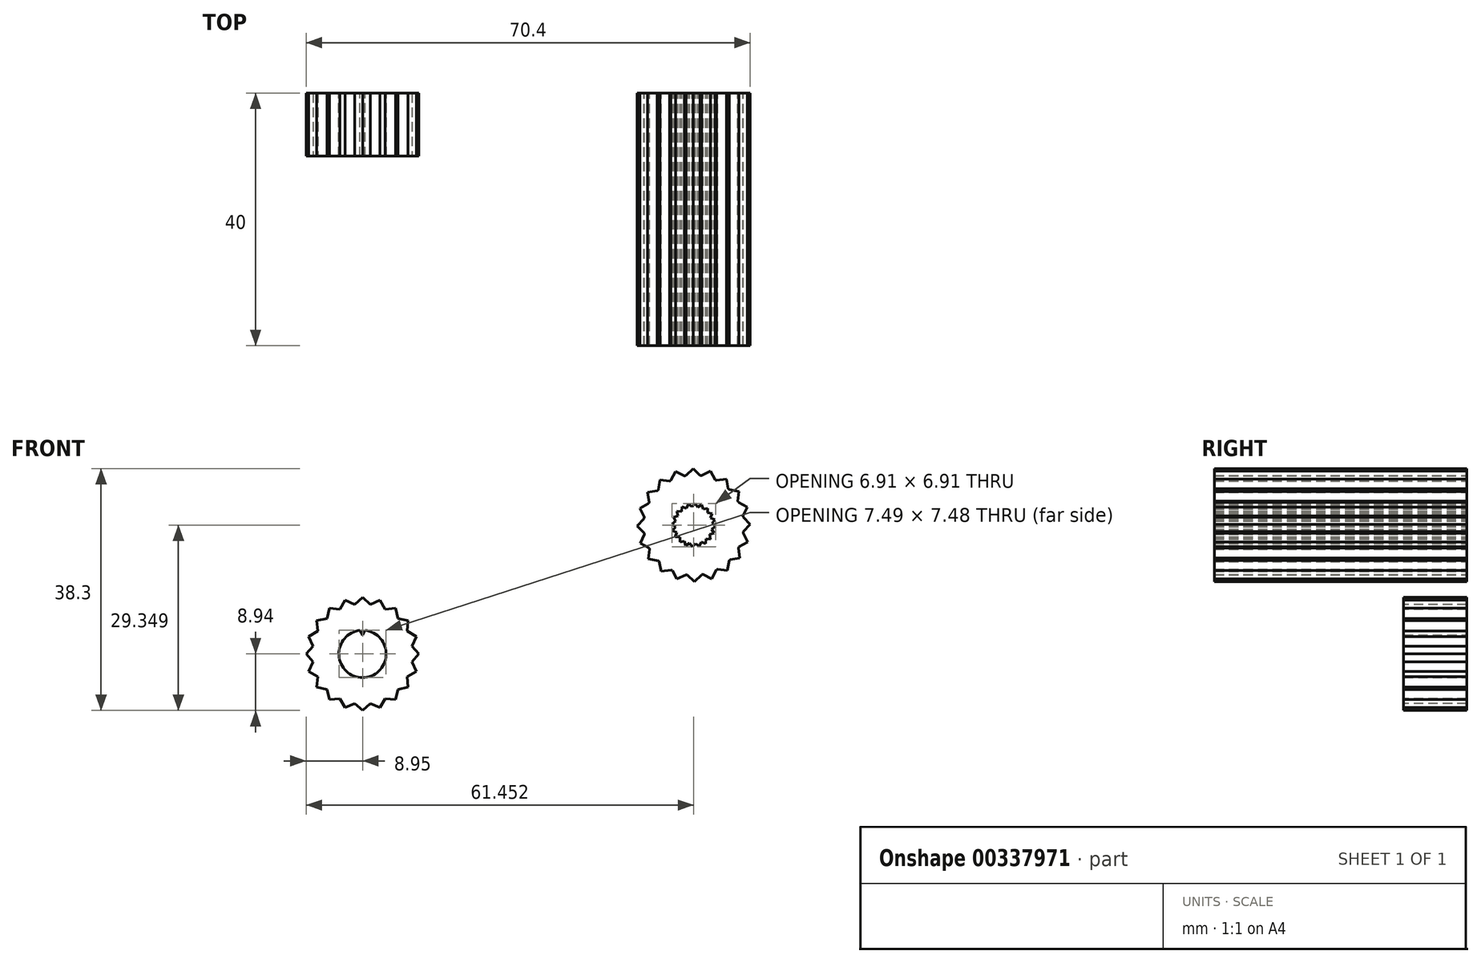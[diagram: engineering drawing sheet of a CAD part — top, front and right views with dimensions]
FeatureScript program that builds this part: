
annotation { "Feature Type Name" : "Feature", "Feature Type Description" : "" }
export const myFeature = defineFeature(function(context is Context, id is Id, definition is map)
    precondition{}
    {
        {
            var Q0;
            Q0=qCreatedBy(makeId("Front.planeOp"),FACE);
            var sketch = newSketch(context, id + "F0", { "sketchPlane" : qUnion([Q0])});
            skCircle(sketch, "E0", {"center": v(0, 0) * mm, "radius": 3 * mm});
            skCircle(sketch, "E1", {"center": v(0, 0) * mm, "radius": 7.95 * mm});
            skCircle(sketch, "E2", {"center": v(0, 0) * mm, "radius": 3.75 * mm});
            skCircle(sketch, "E3", {"center": v(0, 0) * mm, "radius": 8.95 * mm, "construction": true});
            skLineSegment(sketch, "E4", {"start": v(0, 8.95) * mm, "end": v(0, 0) * mm, "construction": true});
            skSolve(sketch);
        }
        {
            var Q0;
            Q0=makeQuery(id+"F0.imprint","IMPRINT",FACE,{"disambiguationData":[TD([[makeQuery(id+"F0.imprint","IMPRINT",EDGE,{"derivedFrom":sQuery(id+"F0.wireOp",EDGE,"E2")}),-1.0]])]});
            extrude(context, id + "F1", {"entities" : qUnion([Q0]), "depth" : 10 * mm});
        }
        {
            var Q0;
            Q0=makeQuery(id+"F1.opExtrude","CAP_FACE",FACE,{"disambiguationData":[OSD([sQuery(id+"F0.wireOp",EDGE,"E1"),sQuery(id+"F0.wireOp",EDGE,"E2")])],"isStart":false});
            var sketch = newSketch(context, id + "F2", { "sketchPlane" : qUnion([Q0])});
            skLineSegment(sketch, "E5", {"start": v(0, 7.95) * mm, "end": v(0, 0) * mm, "construction": true});
            skCircle(sketch, "E6.0", {"center": v(0, 0) * mm, "radius": 7.95 * mm});
            skLineSegment(sketch, "E7", {"start": v(-1.24, 7.85) * mm, "end": v(0, 8.95) * mm});
            skLineSegment(sketch, "E8", {"start": v(0, 8.95) * mm, "end": v(1.24, 7.85) * mm});
            skLineSegment(sketch, "E9", {"start": v(1.24, 7.85) * mm, "end": v(-1.24, 7.85) * mm});
            skLineSegment(sketch, "E10", {"start": v(0, 0) * mm, "end": v(-1.24, 7.85) * mm, "construction": true});
            skLineSegment(sketch, "E11", {"start": v(0, 0) * mm, "end": v(1.24, 7.85) * mm, "construction": true});
            skCircle(sketch, "E12", {"center": v(0, 0) * mm, "radius": 8.95 * mm, "construction": true});
            skLineSegment(sketch, "E13.1.0", {"start": v(-3.58, 7.06) * mm, "end": v(-2.74, 8.49) * mm});
            skLineSegment(sketch, "E13.1.1", {"start": v(-1.21, 7.83) * mm, "end": v(-3.58, 7.06) * mm});
            skLineSegment(sketch, "E13.1.2", {"start": v(-2.74, 8.49) * mm, "end": v(-1.21, 7.83) * mm});
            skLineSegment(sketch, "E13.2.0", {"start": v(-5.56, 5.59) * mm, "end": v(-5.2, 7.2) * mm});
            skLineSegment(sketch, "E13.2.1", {"start": v(-3.55, 7.05) * mm, "end": v(-5.56, 5.59) * mm});
            skLineSegment(sketch, "E13.2.2", {"start": v(-5.2, 7.2) * mm, "end": v(-3.55, 7.05) * mm});
            skLineSegment(sketch, "E13.3.0", {"start": v(-6.98, 3.57) * mm, "end": v(-7.14, 5.22) * mm});
            skLineSegment(sketch, "E13.3.1", {"start": v(-5.52, 5.59) * mm, "end": v(-6.98, 3.57) * mm});
            skLineSegment(sketch, "E13.3.2", {"start": v(-7.14, 5.22) * mm, "end": v(-5.52, 5.59) * mm});
            skLineSegment(sketch, "E13.4.0", {"start": v(-7.72, 1.22) * mm, "end": v(-8.38, 2.74) * mm});
            skLineSegment(sketch, "E13.4.1", {"start": v(-6.95, 3.58) * mm, "end": v(-7.72, 1.22) * mm});
            skLineSegment(sketch, "E13.4.2", {"start": v(-8.38, 2.74) * mm, "end": v(-6.95, 3.58) * mm});
            skLineSegment(sketch, "E13.5.0", {"start": v(-7.69, -1.25) * mm, "end": v(-8.78, 0) * mm});
            skLineSegment(sketch, "E13.5.1", {"start": v(-7.69, 1.24) * mm, "end": v(-7.69, -1.25) * mm});
            skLineSegment(sketch, "E13.5.2", {"start": v(-8.78, 0) * mm, "end": v(-7.69, 1.24) * mm});
            skLineSegment(sketch, "E13.6.0", {"start": v(-6.9, -3.59) * mm, "end": v(-8.32, -2.74) * mm});
            skLineSegment(sketch, "E13.6.1", {"start": v(-7.66, -1.22) * mm, "end": v(-6.9, -3.59) * mm});
            skLineSegment(sketch, "E13.6.2", {"start": v(-8.32, -2.74) * mm, "end": v(-7.66, -1.22) * mm});
            skLineSegment(sketch, "E13.7.0", {"start": v(-5.42, -5.56) * mm, "end": v(-7.04, -5.2) * mm});
            skLineSegment(sketch, "E13.7.1", {"start": v(-6.88, -3.55) * mm, "end": v(-5.42, -5.56) * mm});
            skLineSegment(sketch, "E13.7.2", {"start": v(-7.04, -5.2) * mm, "end": v(-6.88, -3.55) * mm});
            skLineSegment(sketch, "E13.8.0", {"start": v(-3.4, -6.99) * mm, "end": v(-5.06, -7.15) * mm});
            skLineSegment(sketch, "E13.8.1", {"start": v(-5.42, -5.53) * mm, "end": v(-3.4, -6.99) * mm});
            skLineSegment(sketch, "E13.8.2", {"start": v(-5.06, -7.15) * mm, "end": v(-5.42, -5.53) * mm});
            skLineSegment(sketch, "E13.9.0", {"start": v(-1.05, -7.72) * mm, "end": v(-2.57, -8.38) * mm});
            skLineSegment(sketch, "E13.9.1", {"start": v(-3.42, -6.95) * mm, "end": v(-1.05, -7.72) * mm});
            skLineSegment(sketch, "E13.9.2", {"start": v(-2.57, -8.38) * mm, "end": v(-3.42, -6.95) * mm});
            skLineSegment(sketch, "E13.10.0", {"start": v(1.41, -7.7) * mm, "end": v(0.17, -8.79) * mm});
            skLineSegment(sketch, "E13.10.1", {"start": v(-1.07, -7.7) * mm, "end": v(1.41, -7.7) * mm});
            skLineSegment(sketch, "E13.10.2", {"start": v(0.17, -8.79) * mm, "end": v(-1.07, -7.7) * mm});
            skLineSegment(sketch, "E13.11.0", {"start": v(3.75, -6.9) * mm, "end": v(2.9, -8.33) * mm});
            skLineSegment(sketch, "E13.11.1", {"start": v(1.39, -7.67) * mm, "end": v(3.75, -6.9) * mm});
            skLineSegment(sketch, "E13.11.2", {"start": v(2.9, -8.33) * mm, "end": v(1.39, -7.67) * mm});
            skLineSegment(sketch, "E13.12.0", {"start": v(5.73, -5.43) * mm, "end": v(5.37, -7.04) * mm});
            skLineSegment(sketch, "E13.12.1", {"start": v(3.72, -6.89) * mm, "end": v(5.73, -5.43) * mm});
            skLineSegment(sketch, "E13.12.2", {"start": v(5.37, -7.04) * mm, "end": v(3.72, -6.89) * mm});
            skLineSegment(sketch, "E13.13.0", {"start": v(7.15, -3.41) * mm, "end": v(7.31, -5.06) * mm});
            skLineSegment(sketch, "E13.13.1", {"start": v(5.7, -5.42) * mm, "end": v(7.15, -3.41) * mm});
            skLineSegment(sketch, "E13.13.2", {"start": v(7.31, -5.06) * mm, "end": v(5.7, -5.42) * mm});
            skLineSegment(sketch, "E13.14.0", {"start": v(7.89, -1.06) * mm, "end": v(8.55, -2.58) * mm});
            skLineSegment(sketch, "E13.14.1", {"start": v(7.12, -3.42) * mm, "end": v(7.89, -1.06) * mm});
            skLineSegment(sketch, "E13.14.2", {"start": v(8.55, -2.58) * mm, "end": v(7.12, -3.42) * mm});
            skLineSegment(sketch, "E13.15.0", {"start": v(7.86, 1.4) * mm, "end": v(8.96, 0.17) * mm});
            skLineSegment(sketch, "E13.15.1", {"start": v(7.86, -1.08) * mm, "end": v(7.86, 1.4) * mm});
            skLineSegment(sketch, "E13.15.2", {"start": v(8.96, 0.17) * mm, "end": v(7.86, -1.08) * mm});
            skLineSegment(sketch, "E13.16.0", {"start": v(7.07, 3.75) * mm, "end": v(8.5, 2.9) * mm});
            skLineSegment(sketch, "E13.16.1", {"start": v(7.83, 1.38) * mm, "end": v(7.07, 3.75) * mm});
            skLineSegment(sketch, "E13.16.2", {"start": v(8.5, 2.9) * mm, "end": v(7.83, 1.38) * mm});
            skLineSegment(sketch, "E13.17.0", {"start": v(5.6, 5.72) * mm, "end": v(7.21, 5.36) * mm});
            skLineSegment(sketch, "E13.17.1", {"start": v(7.05, 3.71) * mm, "end": v(5.6, 5.72) * mm});
            skLineSegment(sketch, "E13.17.2", {"start": v(7.21, 5.36) * mm, "end": v(7.05, 3.71) * mm});
            skLineSegment(sketch, "E13.18.0", {"start": v(3.58, 7.15) * mm, "end": v(5.23, 7.3) * mm});
            skLineSegment(sketch, "E13.18.1", {"start": v(5.6, 5.69) * mm, "end": v(3.58, 7.15) * mm});
            skLineSegment(sketch, "E13.18.2", {"start": v(5.23, 7.3) * mm, "end": v(5.6, 5.69) * mm});
            skLineSegment(sketch, "E13.19.0", {"start": v(1.22, 7.88) * mm, "end": v(2.74, 8.54) * mm});
            skLineSegment(sketch, "E13.19.1", {"start": v(3.59, 7.11) * mm, "end": v(1.22, 7.88) * mm});
            skLineSegment(sketch, "E13.19.2", {"start": v(2.74, 8.54) * mm, "end": v(3.59, 7.11) * mm});
            skPoint(sketch, "E13.center", {"position": v(0.09, 0.08) * mm});
            skSolve(sketch);
        }
        {
            var Q0;
            {var subQ1=sQuery(id+"F2.wireOp",EDGE,"E7");Q0=makeQuery(id+"F2.imprint","IMPRINT",FACE,{"disambiguationData":[TD([[makeQuery(id+"F2.imprint","IMPRINT",EDGE,{"derivedFrom":subQ1}),-1.0]])]});}
            var Q1;
            Q1=makeQuery(id+"F1.opExtrude","CAP_FACE",FACE,{"disambiguationData":[OSD([sQuery(id+"F0.wireOp",EDGE,"E1"),sQuery(id+"F0.wireOp",EDGE,"E2")])],"isStart":true});
            extrude(context, id + "F3", {"entities" : qUnion([Q0]), "operationType" : NewBodyOperationType.ADD, "endBound" : BoundingType.UP_TO_SURFACE, "oppositeDirection" : true, "endBoundEntityFace" : qUnion([Q1]), "depth" : 25.4 * mm});
        }
        {
            var Q0;
            Q0=makeQuery(id+"F1.opExtrude","SWEPT_BODY",BODY,{"disambiguationData":[OSD([sQuery(id+"F0.wireOp",EDGE,"E1"),sQuery(id+"F0.wireOp",EDGE,"E2")])]});
            var Q1;
            Q1=makeQuery(id+"F1.opExtrude","SWEPT_FACE",FACE,{"disambiguationData":[OSD([sQuery(id+"F0.wireOp",EDGE,"E2")])]});
            circularPattern(context, id + "F4", {"operationType" : NewBodyOperationType.ADD, "entities" : qUnion([Q0]), "axis" : qUnion([Q1]), "angle" : 360 * degree, "instanceCount" : 20, "equalSpace" : true});
        }
        {
            var Q0;
            {var subQ0=sQuery(id+"F0.wireOp",EDGE,"E2");var subQ1=sQuery(id+"F0.wireOp",EDGE,"E1");var subQ2=makeQuery(id+"F3.boolean.opBoolean","MERGE",FACE,{"derivedFrom":[makeQuery(id+"F1.opExtrude","CAP_FACE",FACE,{"disambiguationData":[OSD([subQ1,subQ0])],"isStart":true}),makeQuery(id+"F3.opExtrude","CAP_FACE",FACE,{"disambiguationData":[OSD([subQ1,subQ0])],"isStart":false})]});Q0=makeQuery(id+"F4.boolean.opBoolean","MERGE",FACE,{"derivedFrom":[subQ2,makeQuery(id+"F4.opPattern","COPY",FACE,{"derivedFrom":subQ2,"instanceName":"1"}),makeQuery(id+"F4.opPattern","COPY",FACE,{"derivedFrom":subQ2,"instanceName":"2"}),makeQuery(id+"F4.opPattern","COPY",FACE,{"derivedFrom":subQ2,"instanceName":"3"}),makeQuery(id+"F4.opPattern","COPY",FACE,{"derivedFrom":subQ2,"instanceName":"4"}),makeQuery(id+"F4.opPattern","COPY",FACE,{"derivedFrom":subQ2,"instanceName":"5"}),makeQuery(id+"F4.opPattern","COPY",FACE,{"derivedFrom":subQ2,"instanceName":"6"}),makeQuery(id+"F4.opPattern","COPY",FACE,{"derivedFrom":subQ2,"instanceName":"7"}),makeQuery(id+"F4.opPattern","COPY",FACE,{"derivedFrom":subQ2,"instanceName":"8"}),makeQuery(id+"F4.opPattern","COPY",FACE,{"derivedFrom":subQ2,"instanceName":"9"}),makeQuery(id+"F4.opPattern","COPY",FACE,{"derivedFrom":subQ2,"instanceName":"10"}),makeQuery(id+"F4.opPattern","COPY",FACE,{"derivedFrom":subQ2,"instanceName":"11"}),makeQuery(id+"F4.opPattern","COPY",FACE,{"derivedFrom":subQ2,"instanceName":"12"}),makeQuery(id+"F4.opPattern","COPY",FACE,{"derivedFrom":subQ2,"instanceName":"13"}),makeQuery(id+"F4.opPattern","COPY",FACE,{"derivedFrom":subQ2,"instanceName":"14"}),makeQuery(id+"F4.opPattern","COPY",FACE,{"derivedFrom":subQ2,"instanceName":"15"}),makeQuery(id+"F4.opPattern","COPY",FACE,{"derivedFrom":subQ2,"instanceName":"16"}),makeQuery(id+"F4.opPattern","COPY",FACE,{"derivedFrom":subQ2,"instanceName":"17"}),makeQuery(id+"F4.opPattern","COPY",FACE,{"derivedFrom":subQ2,"instanceName":"18"}),makeQuery(id+"F4.opPattern","COPY",FACE,{"derivedFrom":subQ2,"instanceName":"19"}),makeQuery(id+"F4.opPattern","COPY",FACE,{"derivedFrom":subQ2,"instanceName":"20"}),makeQuery(id+"F4.opPattern","COPY",FACE,{"derivedFrom":subQ2,"instanceName":"21"}),makeQuery(id+"F4.opPattern","COPY",FACE,{"derivedFrom":subQ2,"instanceName":"22"}),makeQuery(id+"F4.opPattern","COPY",FACE,{"derivedFrom":subQ2,"instanceName":"23"}),makeQuery(id+"F4.opPattern","COPY",FACE,{"derivedFrom":subQ2,"instanceName":"24"}),makeQuery(id+"F4.opPattern","COPY",FACE,{"derivedFrom":subQ2,"instanceName":"25"}),makeQuery(id+"F4.opPattern","COPY",FACE,{"derivedFrom":subQ2,"instanceName":"26"}),makeQuery(id+"F4.opPattern","COPY",FACE,{"derivedFrom":subQ2,"instanceName":"27"}),makeQuery(id+"F4.opPattern","COPY",FACE,{"derivedFrom":subQ2,"instanceName":"28"}),makeQuery(id+"F4.opPattern","COPY",FACE,{"derivedFrom":subQ2,"instanceName":"29"})]});}
            var sketch = newSketch(context, id + "F5", { "sketchPlane" : qUnion([Q0])});
            skPoint(sketch, "E14.0", {"position": v(0, 0) * mm});
            skCircle(sketch, "E15", {"center": v(0, 0) * mm, "radius": 3 * mm, "construction": true});
            skLineSegment(sketch, "E16", {"start": v(0, 0) * mm, "end": v(0, 3.75) * mm, "construction": true});
            skLineSegment(sketch, "E17", {"start": v(0, 3) * mm, "end": v(-0.4, 3.73) * mm});
            skLineSegment(sketch, "E18", {"start": v(-0.4, 3.73) * mm, "end": v(0, 4.06) * mm});
            skLineSegment(sketch, "E19", {"start": v(0, 4.06) * mm, "end": v(0.4, 3.73) * mm});
            skLineSegment(sketch, "E20", {"start": v(0.4, 3.73) * mm, "end": v(0, 3) * mm});
            skLineSegment(sketch, "E21", {"start": v(0, 0) * mm, "end": v(-0.4, 3.73) * mm, "construction": true});
            skLineSegment(sketch, "E22.1.0", {"start": v(-0.78, 3.67) * mm, "end": v(-0.93, 2.85) * mm});
            skLineSegment(sketch, "E22.1.1", {"start": v(-0.93, 2.85) * mm, "end": v(-1.53, 3.43) * mm});
            skLineSegment(sketch, "E22.1.2", {"start": v(-1.53, 3.43) * mm, "end": v(-1.26, 3.87) * mm});
            skLineSegment(sketch, "E22.1.3", {"start": v(-1.26, 3.87) * mm, "end": v(-0.78, 3.67) * mm});
            skLineSegment(sketch, "E22.2.0", {"start": v(-1.88, 3.25) * mm, "end": v(-1.76, 2.43) * mm});
            skLineSegment(sketch, "E22.2.1", {"start": v(-1.76, 2.43) * mm, "end": v(-2.5, 2.79) * mm});
            skLineSegment(sketch, "E22.2.2", {"start": v(-2.5, 2.79) * mm, "end": v(-2.39, 3.29) * mm});
            skLineSegment(sketch, "E22.2.3", {"start": v(-2.39, 3.29) * mm, "end": v(-1.88, 3.25) * mm});
            skLineSegment(sketch, "E22.3.0", {"start": v(-2.79, 2.5) * mm, "end": v(-2.43, 1.76) * mm});
            skLineSegment(sketch, "E22.3.1", {"start": v(-2.43, 1.76) * mm, "end": v(-3.25, 1.88) * mm});
            skLineSegment(sketch, "E22.3.2", {"start": v(-3.25, 1.88) * mm, "end": v(-3.29, 2.39) * mm});
            skLineSegment(sketch, "E22.3.3", {"start": v(-3.29, 2.39) * mm, "end": v(-2.79, 2.5) * mm});
            skLineSegment(sketch, "E22.4.0", {"start": v(-3.43, 1.53) * mm, "end": v(-2.85, 0.93) * mm});
            skLineSegment(sketch, "E22.4.1", {"start": v(-2.85, 0.93) * mm, "end": v(-3.67, 0.78) * mm});
            skLineSegment(sketch, "E22.4.2", {"start": v(-3.67, 0.78) * mm, "end": v(-3.87, 1.26) * mm});
            skLineSegment(sketch, "E22.4.3", {"start": v(-3.87, 1.26) * mm, "end": v(-3.43, 1.53) * mm});
            skLineSegment(sketch, "E22.5.0", {"start": v(-3.73, 0.4) * mm, "end": v(-3, 0) * mm});
            skLineSegment(sketch, "E22.5.1", {"start": v(-3, 0) * mm, "end": v(-3.73, -0.4) * mm});
            skLineSegment(sketch, "E22.5.2", {"start": v(-3.73, -0.4) * mm, "end": v(-4.06, 0) * mm});
            skLineSegment(sketch, "E22.5.3", {"start": v(-4.06, 0) * mm, "end": v(-3.73, 0.4) * mm});
            skLineSegment(sketch, "E22.6.0", {"start": v(-3.67, -0.78) * mm, "end": v(-2.85, -0.93) * mm});
            skLineSegment(sketch, "E22.6.1", {"start": v(-2.85, -0.93) * mm, "end": v(-3.43, -1.53) * mm});
            skLineSegment(sketch, "E22.6.2", {"start": v(-3.43, -1.53) * mm, "end": v(-3.87, -1.26) * mm});
            skLineSegment(sketch, "E22.6.3", {"start": v(-3.87, -1.26) * mm, "end": v(-3.67, -0.78) * mm});
            skLineSegment(sketch, "E22.7.0", {"start": v(-3.25, -1.87) * mm, "end": v(-2.43, -1.76) * mm});
            skLineSegment(sketch, "E22.7.1", {"start": v(-2.43, -1.76) * mm, "end": v(-2.79, -2.5) * mm});
            skLineSegment(sketch, "E22.7.2", {"start": v(-2.79, -2.5) * mm, "end": v(-3.29, -2.39) * mm});
            skLineSegment(sketch, "E22.7.3", {"start": v(-3.29, -2.39) * mm, "end": v(-3.25, -1.87) * mm});
            skLineSegment(sketch, "E22.8.0", {"start": v(-2.5, -2.79) * mm, "end": v(-1.76, -2.43) * mm});
            skLineSegment(sketch, "E22.8.1", {"start": v(-1.76, -2.43) * mm, "end": v(-1.88, -3.25) * mm});
            skLineSegment(sketch, "E22.8.2", {"start": v(-1.88, -3.25) * mm, "end": v(-2.39, -3.29) * mm});
            skLineSegment(sketch, "E22.8.3", {"start": v(-2.39, -3.29) * mm, "end": v(-2.5, -2.79) * mm});
            skLineSegment(sketch, "E22.9.0", {"start": v(-1.53, -3.43) * mm, "end": v(-0.93, -2.85) * mm});
            skLineSegment(sketch, "E22.9.1", {"start": v(-0.93, -2.85) * mm, "end": v(-0.78, -3.67) * mm});
            skLineSegment(sketch, "E22.9.2", {"start": v(-0.78, -3.67) * mm, "end": v(-1.26, -3.87) * mm});
            skLineSegment(sketch, "E22.9.3", {"start": v(-1.26, -3.87) * mm, "end": v(-1.53, -3.43) * mm});
            skLineSegment(sketch, "E22.10.0", {"start": v(-0.4, -3.73) * mm, "end": v(0, -3) * mm});
            skLineSegment(sketch, "E22.10.1", {"start": v(0, -3) * mm, "end": v(0.4, -3.73) * mm});
            skLineSegment(sketch, "E22.10.2", {"start": v(0.4, -3.73) * mm, "end": v(0, -4.06) * mm});
            skLineSegment(sketch, "E22.10.3", {"start": v(0, -4.06) * mm, "end": v(-0.4, -3.73) * mm});
            skLineSegment(sketch, "E22.11.0", {"start": v(0.78, -3.67) * mm, "end": v(0.93, -2.85) * mm});
            skLineSegment(sketch, "E22.11.1", {"start": v(0.93, -2.85) * mm, "end": v(1.53, -3.43) * mm});
            skLineSegment(sketch, "E22.11.2", {"start": v(1.53, -3.43) * mm, "end": v(1.26, -3.87) * mm});
            skLineSegment(sketch, "E22.11.3", {"start": v(1.26, -3.87) * mm, "end": v(0.78, -3.67) * mm});
            skLineSegment(sketch, "E22.12.0", {"start": v(1.87, -3.25) * mm, "end": v(1.76, -2.43) * mm});
            skLineSegment(sketch, "E22.12.1", {"start": v(1.76, -2.43) * mm, "end": v(2.5, -2.79) * mm});
            skLineSegment(sketch, "E22.12.2", {"start": v(2.5, -2.79) * mm, "end": v(2.39, -3.29) * mm});
            skLineSegment(sketch, "E22.12.3", {"start": v(2.39, -3.29) * mm, "end": v(1.87, -3.25) * mm});
            skLineSegment(sketch, "E22.13.0", {"start": v(2.79, -2.5) * mm, "end": v(2.43, -1.76) * mm});
            skLineSegment(sketch, "E22.13.1", {"start": v(2.43, -1.76) * mm, "end": v(3.25, -1.88) * mm});
            skLineSegment(sketch, "E22.13.2", {"start": v(3.25, -1.88) * mm, "end": v(3.29, -2.39) * mm});
            skLineSegment(sketch, "E22.13.3", {"start": v(3.29, -2.39) * mm, "end": v(2.79, -2.5) * mm});
            skLineSegment(sketch, "E22.14.0", {"start": v(3.43, -1.53) * mm, "end": v(2.85, -0.93) * mm});
            skLineSegment(sketch, "E22.14.1", {"start": v(2.85, -0.93) * mm, "end": v(3.67, -0.78) * mm});
            skLineSegment(sketch, "E22.14.2", {"start": v(3.67, -0.78) * mm, "end": v(3.87, -1.26) * mm});
            skLineSegment(sketch, "E22.14.3", {"start": v(3.87, -1.26) * mm, "end": v(3.43, -1.53) * mm});
            skLineSegment(sketch, "E22.15.0", {"start": v(3.73, -0.4) * mm, "end": v(3, 0) * mm});
            skLineSegment(sketch, "E22.15.1", {"start": v(3, 0) * mm, "end": v(3.73, 0.4) * mm});
            skLineSegment(sketch, "E22.15.2", {"start": v(3.73, 0.4) * mm, "end": v(4.06, 0) * mm});
            skLineSegment(sketch, "E22.15.3", {"start": v(4.06, 0) * mm, "end": v(3.73, -0.4) * mm});
            skLineSegment(sketch, "E22.16.0", {"start": v(3.67, 0.78) * mm, "end": v(2.85, 0.93) * mm});
            skLineSegment(sketch, "E22.16.1", {"start": v(2.85, 0.93) * mm, "end": v(3.43, 1.53) * mm});
            skLineSegment(sketch, "E22.16.2", {"start": v(3.43, 1.53) * mm, "end": v(3.87, 1.26) * mm});
            skLineSegment(sketch, "E22.16.3", {"start": v(3.87, 1.26) * mm, "end": v(3.67, 0.78) * mm});
            skLineSegment(sketch, "E22.17.0", {"start": v(3.25, 1.87) * mm, "end": v(2.43, 1.76) * mm});
            skLineSegment(sketch, "E22.17.1", {"start": v(2.43, 1.76) * mm, "end": v(2.79, 2.5) * mm});
            skLineSegment(sketch, "E22.17.2", {"start": v(2.79, 2.5) * mm, "end": v(3.29, 2.39) * mm});
            skLineSegment(sketch, "E22.17.3", {"start": v(3.29, 2.39) * mm, "end": v(3.25, 1.87) * mm});
            skLineSegment(sketch, "E22.18.0", {"start": v(2.5, 2.79) * mm, "end": v(1.76, 2.43) * mm});
            skLineSegment(sketch, "E22.18.1", {"start": v(1.76, 2.43) * mm, "end": v(1.88, 3.25) * mm});
            skLineSegment(sketch, "E22.18.2", {"start": v(1.88, 3.25) * mm, "end": v(2.39, 3.29) * mm});
            skLineSegment(sketch, "E22.18.3", {"start": v(2.39, 3.29) * mm, "end": v(2.5, 2.79) * mm});
            skLineSegment(sketch, "E22.19.0", {"start": v(1.53, 3.43) * mm, "end": v(0.93, 2.85) * mm});
            skLineSegment(sketch, "E22.19.1", {"start": v(0.93, 2.85) * mm, "end": v(0.78, 3.67) * mm});
            skLineSegment(sketch, "E22.19.2", {"start": v(0.78, 3.67) * mm, "end": v(1.26, 3.87) * mm});
            skLineSegment(sketch, "E22.19.3", {"start": v(1.26, 3.87) * mm, "end": v(1.53, 3.43) * mm});
            skSolve(sketch);
        }
        {
            var Q0;
            {var subQ0=sQuery(id+"F5.wireOp",EDGE,"E17");Q0=makeQuery(id+"F5.imprint","IMPRINT",FACE,{"disambiguationData":[TD([[makeQuery(id+"F5.imprint","IMPRINT",EDGE,{"derivedFrom":subQ0}),-1.0]])]});}
            var Q1;
            {var subQ0=sQuery(id+"F5.wireOp",EDGE,"E18");Q1=makeQuery(id+"F5.imprint","IMPRINT",FACE,{"disambiguationData":[TD([[makeQuery(id+"F5.imprint","IMPRINT",EDGE,{"derivedFrom":subQ0}),-1.0]])]});}
            var Q2;
            {var subQ0=makeQuery(id+"F3.boolean.opBoolean","MERGE",FACE,{"derivedFrom":[makeQuery(id+"F1.opExtrude","CAP_FACE",FACE,{"disambiguationData":[OSD([sQuery(id+"F0.wireOp",EDGE,"E1"),sQuery(id+"F0.wireOp",EDGE,"E2")])],"isStart":false}),makeQuery(id+"F3.opExtrude","CAP_FACE",FACE,{"disambiguationData":[OSD([sQuery(id+"F2.wireOp",EDGE,"E6.0"),sQuery(id+"F2.wireOp",EDGE,"E7"),sQuery(id+"F2.wireOp",EDGE,"E8")])],"isStart":true})]});Q2=makeQuery(id+"F4.boolean.opBoolean","MERGE",FACE,{"derivedFrom":[subQ0,makeQuery(id+"F4.opPattern","COPY",FACE,{"derivedFrom":subQ0,"instanceName":"1"}),makeQuery(id+"F4.opPattern","COPY",FACE,{"derivedFrom":subQ0,"instanceName":"2"}),makeQuery(id+"F4.opPattern","COPY",FACE,{"derivedFrom":subQ0,"instanceName":"3"}),makeQuery(id+"F4.opPattern","COPY",FACE,{"derivedFrom":subQ0,"instanceName":"4"}),makeQuery(id+"F4.opPattern","COPY",FACE,{"derivedFrom":subQ0,"instanceName":"5"}),makeQuery(id+"F4.opPattern","COPY",FACE,{"derivedFrom":subQ0,"instanceName":"6"}),makeQuery(id+"F4.opPattern","COPY",FACE,{"derivedFrom":subQ0,"instanceName":"7"}),makeQuery(id+"F4.opPattern","COPY",FACE,{"derivedFrom":subQ0,"instanceName":"8"}),makeQuery(id+"F4.opPattern","COPY",FACE,{"derivedFrom":subQ0,"instanceName":"9"}),makeQuery(id+"F4.opPattern","COPY",FACE,{"derivedFrom":subQ0,"instanceName":"10"}),makeQuery(id+"F4.opPattern","COPY",FACE,{"derivedFrom":subQ0,"instanceName":"11"}),makeQuery(id+"F4.opPattern","COPY",FACE,{"derivedFrom":subQ0,"instanceName":"12"}),makeQuery(id+"F4.opPattern","COPY",FACE,{"derivedFrom":subQ0,"instanceName":"13"}),makeQuery(id+"F4.opPattern","COPY",FACE,{"derivedFrom":subQ0,"instanceName":"14"}),makeQuery(id+"F4.opPattern","COPY",FACE,{"derivedFrom":subQ0,"instanceName":"15"}),makeQuery(id+"F4.opPattern","COPY",FACE,{"derivedFrom":subQ0,"instanceName":"16"}),makeQuery(id+"F4.opPattern","COPY",FACE,{"derivedFrom":subQ0,"instanceName":"17"}),makeQuery(id+"F4.opPattern","COPY",FACE,{"derivedFrom":subQ0,"instanceName":"18"}),makeQuery(id+"F4.opPattern","COPY",FACE,{"derivedFrom":subQ0,"instanceName":"19"}),makeQuery(id+"F4.opPattern","COPY",FACE,{"derivedFrom":subQ0,"instanceName":"20"}),makeQuery(id+"F4.opPattern","COPY",FACE,{"derivedFrom":subQ0,"instanceName":"21"}),makeQuery(id+"F4.opPattern","COPY",FACE,{"derivedFrom":subQ0,"instanceName":"22"}),makeQuery(id+"F4.opPattern","COPY",FACE,{"derivedFrom":subQ0,"instanceName":"23"}),makeQuery(id+"F4.opPattern","COPY",FACE,{"derivedFrom":subQ0,"instanceName":"24"}),makeQuery(id+"F4.opPattern","COPY",FACE,{"derivedFrom":subQ0,"instanceName":"25"}),makeQuery(id+"F4.opPattern","COPY",FACE,{"derivedFrom":subQ0,"instanceName":"26"}),makeQuery(id+"F4.opPattern","COPY",FACE,{"derivedFrom":subQ0,"instanceName":"27"}),makeQuery(id+"F4.opPattern","COPY",FACE,{"derivedFrom":subQ0,"instanceName":"28"}),makeQuery(id+"F4.opPattern","COPY",FACE,{"derivedFrom":subQ0,"instanceName":"29"})]});}
            extrude(context, id + "F6", {"entities" : qUnion([Q0, Q1]), "operationType" : NewBodyOperationType.ADD, "endBound" : BoundingType.UP_TO_SURFACE, "oppositeDirection" : true, "endBoundEntityFace" : qUnion([Q2]), "depth" : 25.4 * mm});
        }
        {
            var Q0;
            Q0=qCreatedBy(makeId("Front.planeOp"),FACE);
            var sketch = newSketch(context, id + "F7", { "sketchPlane" : qUnion([Q0])});
            skPoint(sketch, "E23", {"position": v(52.5, 20.4) * mm});
            skLineSegment(sketch, "E24", {"start": v(51.12, 23.58) * mm, "end": v(52.5, 20.4) * mm, "construction": true});
            skLineSegment(sketch, "E25", {"start": v(51.64, 23.76) * mm, "end": v(51.34, 23.08) * mm});
            skLineSegment(sketch, "E26", {"start": v(51.34, 23.08) * mm, "end": v(50.63, 23.33) * mm});
            skCircle(sketch, "E27", {"center": v(52.5, 20.4) * mm, "radius": 3.5 * mm});
            skLineSegment(sketch, "E28.1.1", {"start": v(50.57, 22.59) * mm, "end": v(49.82, 22.6) * mm});
            skLineSegment(sketch, "E28.1.2", {"start": v(50.65, 23.33) * mm, "end": v(50.57, 22.59) * mm});
            skLineSegment(sketch, "E28.2.1", {"start": v(49.99, 21.88) * mm, "end": v(49.27, 21.67) * mm});
            skLineSegment(sketch, "E28.2.2", {"start": v(49.83, 22.61) * mm, "end": v(49.99, 21.88) * mm});
            skLineSegment(sketch, "E28.3.1", {"start": v(49.65, 21.03) * mm, "end": v(49.03, 20.6) * mm});
            skLineSegment(sketch, "E28.3.2", {"start": v(49.28, 21.68) * mm, "end": v(49.65, 21.03) * mm});
            skLineSegment(sketch, "E28.4.1", {"start": v(49.6, 20.12) * mm, "end": v(49.14, 19.53) * mm});
            skLineSegment(sketch, "E28.4.2", {"start": v(49.04, 20.62) * mm, "end": v(49.6, 20.12) * mm});
            skLineSegment(sketch, "E28.5.1", {"start": v(49.82, 19.23) * mm, "end": v(49.57, 18.53) * mm});
            skLineSegment(sketch, "E28.5.2", {"start": v(49.14, 19.54) * mm, "end": v(49.82, 19.23) * mm});
            skLineSegment(sketch, "E28.6.1", {"start": v(50.32, 18.46) * mm, "end": v(50.3, 17.72) * mm});
            skLineSegment(sketch, "E28.6.2", {"start": v(49.57, 18.54) * mm, "end": v(50.32, 18.46) * mm});
            skLineSegment(sketch, "E28.7.1", {"start": v(51.02, 17.88) * mm, "end": v(51.23, 17.17) * mm});
            skLineSegment(sketch, "E28.7.2", {"start": v(50.29, 17.73) * mm, "end": v(51.02, 17.88) * mm});
            skLineSegment(sketch, "E28.8.1", {"start": v(51.87, 17.55) * mm, "end": v(52.3, 16.93) * mm});
            skLineSegment(sketch, "E28.8.2", {"start": v(51.22, 17.18) * mm, "end": v(51.87, 17.55) * mm});
            skLineSegment(sketch, "E28.9.1", {"start": v(52.78, 17.5) * mm, "end": v(53.37, 17.04) * mm});
            skLineSegment(sketch, "E28.9.2", {"start": v(52.28, 16.94) * mm, "end": v(52.78, 17.5) * mm});
            skLineSegment(sketch, "E28.10.1", {"start": v(53.67, 17.72) * mm, "end": v(54.37, 17.47) * mm});
            skLineSegment(sketch, "E28.10.2", {"start": v(53.36, 17.04) * mm, "end": v(53.67, 17.72) * mm});
            skLineSegment(sketch, "E28.11.1", {"start": v(54.44, 18.21) * mm, "end": v(55.18, 18.2) * mm});
            skLineSegment(sketch, "E28.11.2", {"start": v(54.36, 17.47) * mm, "end": v(54.44, 18.21) * mm});
            skLineSegment(sketch, "E28.12.1", {"start": v(55.02, 18.92) * mm, "end": v(55.74, 19.13) * mm});
            skLineSegment(sketch, "E28.12.2", {"start": v(55.17, 18.19) * mm, "end": v(55.02, 18.92) * mm});
            skLineSegment(sketch, "E28.13.1", {"start": v(55.35, 19.77) * mm, "end": v(55.97, 20.19) * mm});
            skLineSegment(sketch, "E28.13.2", {"start": v(55.72, 19.12) * mm, "end": v(55.35, 19.77) * mm});
            skLineSegment(sketch, "E28.14.1", {"start": v(55.4, 20.68) * mm, "end": v(55.87, 21.27) * mm});
            skLineSegment(sketch, "E28.14.2", {"start": v(55.96, 20.18) * mm, "end": v(55.4, 20.68) * mm});
            skLineSegment(sketch, "E28.15.1", {"start": v(55.18, 21.56) * mm, "end": v(55.43, 22.27) * mm});
            skLineSegment(sketch, "E28.15.2", {"start": v(55.86, 21.26) * mm, "end": v(55.18, 21.56) * mm});
            skLineSegment(sketch, "E28.16.1", {"start": v(54.69, 22.34) * mm, "end": v(54.71, 23.08) * mm});
            skLineSegment(sketch, "E28.16.2", {"start": v(55.43, 22.25) * mm, "end": v(54.69, 22.34) * mm});
            skLineSegment(sketch, "E28.17.1", {"start": v(53.98, 22.92) * mm, "end": v(53.77, 23.63) * mm});
            skLineSegment(sketch, "E28.17.2", {"start": v(54.71, 23.07) * mm, "end": v(53.98, 22.92) * mm});
            skLineSegment(sketch, "E28.18.1", {"start": v(53.13, 23.25) * mm, "end": v(52.71, 23.87) * mm});
            skLineSegment(sketch, "E28.18.2", {"start": v(53.78, 23.62) * mm, "end": v(53.13, 23.25) * mm});
            skLineSegment(sketch, "E28.19.1", {"start": v(52.22, 23.3) * mm, "end": v(51.63, 23.76) * mm});
            skLineSegment(sketch, "E28.19.2", {"start": v(52.72, 23.86) * mm, "end": v(52.22, 23.3) * mm});
            skLineSegment(sketch, "E29", {"start": v(52.42, 28.27) * mm, "end": v(52.5, 20.4) * mm, "construction": true});
            skCircle(sketch, "E30.0", {"center": v(52.5, 20.4) * mm, "radius": 7.95 * mm});
            skLineSegment(sketch, "E31", {"start": v(51.17, 28.17) * mm, "end": v(52.4, 29.35) * mm});
            skLineSegment(sketch, "E32", {"start": v(52.4, 29.35) * mm, "end": v(53.63, 28.17) * mm});
            skLineSegment(sketch, "E33", {"start": v(53.63, 28.17) * mm, "end": v(51.17, 28.17) * mm});
            skLineSegment(sketch, "E34", {"start": v(52.5, 20.4) * mm, "end": v(51.17, 28.17) * mm, "construction": true});
            skLineSegment(sketch, "E35", {"start": v(52.5, 20.4) * mm, "end": v(53.63, 28.17) * mm, "construction": true});
            skCircle(sketch, "E36", {"center": v(52.5, 20.4) * mm, "radius": 8.95 * mm, "construction": true});
            skLineSegment(sketch, "E37.1.0", {"start": v(48.84, 27.38) * mm, "end": v(49.64, 28.88) * mm});
            skLineSegment(sketch, "E37.1.1", {"start": v(51.18, 28.14) * mm, "end": v(48.84, 27.38) * mm});
            skLineSegment(sketch, "E37.1.2", {"start": v(49.64, 28.88) * mm, "end": v(51.18, 28.14) * mm});
            skLineSegment(sketch, "E37.2.0", {"start": v(46.86, 25.9) * mm, "end": v(47.16, 27.58) * mm});
            skLineSegment(sketch, "E37.2.1", {"start": v(48.85, 27.35) * mm, "end": v(46.86, 25.9) * mm});
            skLineSegment(sketch, "E37.2.2", {"start": v(47.16, 27.58) * mm, "end": v(48.85, 27.35) * mm});
            skLineSegment(sketch, "E37.3.0", {"start": v(45.43, 23.9) * mm, "end": v(45.2, 25.58) * mm});
            skLineSegment(sketch, "E37.3.1", {"start": v(46.88, 25.88) * mm, "end": v(45.43, 23.9) * mm});
            skLineSegment(sketch, "E37.3.2", {"start": v(45.2, 25.58) * mm, "end": v(46.88, 25.88) * mm});
            skLineSegment(sketch, "E37.4.0", {"start": v(44.7, 21.54) * mm, "end": v(43.96, 23.07) * mm});
            skLineSegment(sketch, "E37.4.1", {"start": v(45.46, 23.88) * mm, "end": v(44.7, 21.54) * mm});
            skLineSegment(sketch, "E37.4.2", {"start": v(43.96, 23.07) * mm, "end": v(45.46, 23.88) * mm});
            skLineSegment(sketch, "E37.5.0", {"start": v(44.73, 19.07) * mm, "end": v(43.55, 20.3) * mm});
            skLineSegment(sketch, "E37.5.1", {"start": v(44.73, 21.53) * mm, "end": v(44.73, 19.07) * mm});
            skLineSegment(sketch, "E37.5.2", {"start": v(43.55, 20.3) * mm, "end": v(44.73, 21.53) * mm});
            skLineSegment(sketch, "E37.6.0", {"start": v(45.52, 16.73) * mm, "end": v(44.02, 17.54) * mm});
            skLineSegment(sketch, "E37.6.1", {"start": v(44.76, 19.08) * mm, "end": v(45.52, 16.73) * mm});
            skLineSegment(sketch, "E37.6.2", {"start": v(44.02, 17.54) * mm, "end": v(44.76, 19.08) * mm});
            skLineSegment(sketch, "E37.7.0", {"start": v(47, 14.76) * mm, "end": v(45.32, 15.06) * mm});
            skLineSegment(sketch, "E37.7.1", {"start": v(45.55, 16.75) * mm, "end": v(47, 14.76) * mm});
            skLineSegment(sketch, "E37.7.2", {"start": v(45.32, 15.06) * mm, "end": v(45.55, 16.75) * mm});
            skLineSegment(sketch, "E37.8.0", {"start": v(49, 13.33) * mm, "end": v(47.32, 13.1) * mm});
            skLineSegment(sketch, "E37.8.1", {"start": v(47.02, 14.78) * mm, "end": v(49, 13.33) * mm});
            skLineSegment(sketch, "E37.8.2", {"start": v(47.32, 13.1) * mm, "end": v(47.02, 14.78) * mm});
            skLineSegment(sketch, "E37.9.0", {"start": v(51.36, 12.6) * mm, "end": v(49.83, 11.86) * mm});
            skLineSegment(sketch, "E37.9.1", {"start": v(49.02, 13.36) * mm, "end": v(51.36, 12.6) * mm});
            skLineSegment(sketch, "E37.9.2", {"start": v(49.83, 11.86) * mm, "end": v(49.02, 13.36) * mm});
            skLineSegment(sketch, "E37.10.0", {"start": v(53.83, 12.63) * mm, "end": v(52.6, 11.45) * mm});
            skLineSegment(sketch, "E37.10.1", {"start": v(51.37, 12.63) * mm, "end": v(53.83, 12.63) * mm});
            skLineSegment(sketch, "E37.10.2", {"start": v(52.6, 11.45) * mm, "end": v(51.37, 12.63) * mm});
            skLineSegment(sketch, "E37.11.0", {"start": v(56.17, 13.42) * mm, "end": v(55.36, 11.92) * mm});
            skLineSegment(sketch, "E37.11.1", {"start": v(53.83, 12.66) * mm, "end": v(56.17, 13.42) * mm});
            skLineSegment(sketch, "E37.11.2", {"start": v(55.36, 11.92) * mm, "end": v(53.83, 12.66) * mm});
            skLineSegment(sketch, "E37.12.0", {"start": v(58.15, 14.9) * mm, "end": v(57.84, 13.22) * mm});
            skLineSegment(sketch, "E37.12.1", {"start": v(56.15, 13.45) * mm, "end": v(58.15, 14.9) * mm});
            skLineSegment(sketch, "E37.12.2", {"start": v(57.84, 13.22) * mm, "end": v(56.15, 13.45) * mm});
            skLineSegment(sketch, "E37.13.0", {"start": v(59.57, 16.9) * mm, "end": v(59.8, 15.22) * mm});
            skLineSegment(sketch, "E37.13.1", {"start": v(58.12, 14.91) * mm, "end": v(59.57, 16.9) * mm});
            skLineSegment(sketch, "E37.13.2", {"start": v(59.8, 15.22) * mm, "end": v(58.12, 14.91) * mm});
            skLineSegment(sketch, "E37.14.0", {"start": v(60.3, 19.26) * mm, "end": v(61.04, 17.73) * mm});
            skLineSegment(sketch, "E37.14.1", {"start": v(59.54, 16.92) * mm, "end": v(60.3, 19.26) * mm});
            skLineSegment(sketch, "E37.14.2", {"start": v(61.04, 17.73) * mm, "end": v(59.54, 16.92) * mm});
            skLineSegment(sketch, "E37.15.0", {"start": v(60.27, 21.73) * mm, "end": v(61.45, 20.5) * mm});
            skLineSegment(sketch, "E37.15.1", {"start": v(60.27, 19.27) * mm, "end": v(60.27, 21.73) * mm});
            skLineSegment(sketch, "E37.15.2", {"start": v(61.45, 20.5) * mm, "end": v(60.27, 19.27) * mm});
            skLineSegment(sketch, "E37.16.0", {"start": v(59.48, 24.07) * mm, "end": v(60.98, 23.26) * mm});
            skLineSegment(sketch, "E37.16.1", {"start": v(60.24, 21.72) * mm, "end": v(59.48, 24.07) * mm});
            skLineSegment(sketch, "E37.16.2", {"start": v(60.98, 23.26) * mm, "end": v(60.24, 21.72) * mm});
            skLineSegment(sketch, "E37.17.0", {"start": v(58, 26.04) * mm, "end": v(59.68, 25.74) * mm});
            skLineSegment(sketch, "E37.17.1", {"start": v(59.46, 24.05) * mm, "end": v(58, 26.04) * mm});
            skLineSegment(sketch, "E37.17.2", {"start": v(59.68, 25.74) * mm, "end": v(59.46, 24.05) * mm});
            skLineSegment(sketch, "E37.18.0", {"start": v(56, 27.47) * mm, "end": v(57.68, 27.7) * mm});
            skLineSegment(sketch, "E37.18.1", {"start": v(57.99, 26.02) * mm, "end": v(56, 27.47) * mm});
            skLineSegment(sketch, "E37.18.2", {"start": v(57.68, 27.7) * mm, "end": v(57.99, 26.02) * mm});
            skLineSegment(sketch, "E37.19.0", {"start": v(53.64, 28.2) * mm, "end": v(55.17, 28.94) * mm});
            skLineSegment(sketch, "E37.19.1", {"start": v(55.98, 27.44) * mm, "end": v(53.64, 28.2) * mm});
            skLineSegment(sketch, "E37.19.2", {"start": v(55.17, 28.94) * mm, "end": v(55.98, 27.44) * mm});
            skPoint(sketch, "E38", {"position": v(71.51, 12.05) * mm});
            skCircle(sketch, "E39", {"center": v(71.51, 12.05) * mm, "radius": 2.15 * mm});
            skLineSegment(sketch, "E40", {"start": v(71.51, 12.05) * mm, "end": v(72.63, 13.9) * mm, "construction": true});
            skLineSegment(sketch, "E41", {"start": v(72.32, 14.05) * mm, "end": v(72.45, 13.6) * mm});
            skLineSegment(sketch, "E42", {"start": v(72.45, 13.6) * mm, "end": v(72.91, 13.69) * mm});
            skLineSegment(sketch, "E43", {"start": v(72.91, 13.69) * mm, "end": v(72.32, 14.05) * mm});
            skLineSegment(sketch, "E44.1.0", {"start": v(71.93, 13.8) * mm, "end": v(72.34, 14.04) * mm});
            skLineSegment(sketch, "E44.1.1", {"start": v(72.34, 14.04) * mm, "end": v(71.66, 14.2) * mm});
            skLineSegment(sketch, "E44.1.2", {"start": v(71.66, 14.2) * mm, "end": v(71.93, 13.8) * mm});
            skLineSegment(sketch, "E44.2.0", {"start": v(71.36, 13.85) * mm, "end": v(71.68, 14.2) * mm});
            skLineSegment(sketch, "E44.2.1", {"start": v(71.68, 14.2) * mm, "end": v(70.99, 14.14) * mm});
            skLineSegment(sketch, "E44.2.2", {"start": v(70.99, 14.14) * mm, "end": v(71.36, 13.85) * mm});
            skLineSegment(sketch, "E44.3.0", {"start": v(70.82, 13.71) * mm, "end": v(71.01, 14.15) * mm});
            skLineSegment(sketch, "E44.3.1", {"start": v(71.01, 14.15) * mm, "end": v(70.37, 13.88) * mm});
            skLineSegment(sketch, "E44.3.2", {"start": v(70.37, 13.88) * mm, "end": v(70.82, 13.71) * mm});
            skLineSegment(sketch, "E44.4.0", {"start": v(70.34, 13.42) * mm, "end": v(70.4, 13.89) * mm});
            skLineSegment(sketch, "E44.4.1", {"start": v(70.4, 13.89) * mm, "end": v(69.86, 13.43) * mm});
            skLineSegment(sketch, "E44.4.2", {"start": v(69.86, 13.43) * mm, "end": v(70.34, 13.42) * mm});
            skLineSegment(sketch, "E44.5.0", {"start": v(69.97, 12.99) * mm, "end": v(69.88, 13.45) * mm});
            skLineSegment(sketch, "E44.5.1", {"start": v(69.88, 13.45) * mm, "end": v(69.52, 12.86) * mm});
            skLineSegment(sketch, "E44.5.2", {"start": v(69.52, 12.86) * mm, "end": v(69.97, 12.99) * mm});
            skLineSegment(sketch, "E44.6.0", {"start": v(69.76, 12.47) * mm, "end": v(69.52, 12.88) * mm});
            skLineSegment(sketch, "E44.6.1", {"start": v(69.52, 12.88) * mm, "end": v(69.36, 12.2) * mm});
            skLineSegment(sketch, "E44.6.2", {"start": v(69.36, 12.2) * mm, "end": v(69.76, 12.47) * mm});
            skLineSegment(sketch, "E44.7.0", {"start": v(69.72, 11.9) * mm, "end": v(69.37, 12.22) * mm});
            skLineSegment(sketch, "E44.7.1", {"start": v(69.37, 12.22) * mm, "end": v(69.42, 11.53) * mm});
            skLineSegment(sketch, "E44.7.2", {"start": v(69.42, 11.53) * mm, "end": v(69.72, 11.9) * mm});
            skLineSegment(sketch, "E44.8.0", {"start": v(69.85, 11.36) * mm, "end": v(69.42, 11.55) * mm});
            skLineSegment(sketch, "E44.8.1", {"start": v(69.42, 11.55) * mm, "end": v(69.69, 10.9) * mm});
            skLineSegment(sketch, "E44.8.2", {"start": v(69.69, 10.9) * mm, "end": v(69.85, 11.36) * mm});
            skLineSegment(sketch, "E44.9.0", {"start": v(70.15, 10.88) * mm, "end": v(69.67, 10.93) * mm});
            skLineSegment(sketch, "E44.9.1", {"start": v(69.67, 10.93) * mm, "end": v(70.13, 10.4) * mm});
            skLineSegment(sketch, "E44.9.2", {"start": v(70.13, 10.4) * mm, "end": v(70.15, 10.88) * mm});
            skLineSegment(sketch, "E44.10.0", {"start": v(70.58, 10.51) * mm, "end": v(70.11, 10.42) * mm});
            skLineSegment(sketch, "E44.10.1", {"start": v(70.11, 10.42) * mm, "end": v(70.7, 10.05) * mm});
            skLineSegment(sketch, "E44.10.2", {"start": v(70.7, 10.05) * mm, "end": v(70.58, 10.51) * mm});
            skLineSegment(sketch, "E44.11.0", {"start": v(71.1, 10.3) * mm, "end": v(70.68, 10.06) * mm});
            skLineSegment(sketch, "E44.11.1", {"start": v(70.68, 10.06) * mm, "end": v(71.36, 9.9) * mm});
            skLineSegment(sketch, "E44.11.2", {"start": v(71.36, 9.9) * mm, "end": v(71.1, 10.3) * mm});
            skLineSegment(sketch, "E44.12.0", {"start": v(71.66, 10.25) * mm, "end": v(71.34, 9.9) * mm});
            skLineSegment(sketch, "E44.12.1", {"start": v(71.34, 9.9) * mm, "end": v(72.03, 9.96) * mm});
            skLineSegment(sketch, "E44.12.2", {"start": v(72.03, 9.96) * mm, "end": v(71.66, 10.25) * mm});
            skLineSegment(sketch, "E44.13.0", {"start": v(72.2, 10.39) * mm, "end": v(72.01, 9.96) * mm});
            skLineSegment(sketch, "E44.13.1", {"start": v(72.01, 9.96) * mm, "end": v(72.65, 10.23) * mm});
            skLineSegment(sketch, "E44.13.2", {"start": v(72.65, 10.23) * mm, "end": v(72.2, 10.39) * mm});
            skLineSegment(sketch, "E44.14.0", {"start": v(72.69, 10.68) * mm, "end": v(72.63, 10.21) * mm});
            skLineSegment(sketch, "E44.14.1", {"start": v(72.63, 10.21) * mm, "end": v(73.16, 10.67) * mm});
            skLineSegment(sketch, "E44.14.2", {"start": v(73.16, 10.67) * mm, "end": v(72.69, 10.68) * mm});
            skLineSegment(sketch, "E44.15.0", {"start": v(73.05, 11.12) * mm, "end": v(73.15, 10.65) * mm});
            skLineSegment(sketch, "E44.15.1", {"start": v(73.15, 10.65) * mm, "end": v(73.5, 11.25) * mm});
            skLineSegment(sketch, "E44.15.2", {"start": v(73.5, 11.25) * mm, "end": v(73.05, 11.12) * mm});
            skLineSegment(sketch, "E44.16.0", {"start": v(73.27, 11.64) * mm, "end": v(73.5, 11.22) * mm});
            skLineSegment(sketch, "E44.16.1", {"start": v(73.5, 11.22) * mm, "end": v(73.66, 11.9) * mm});
            skLineSegment(sketch, "E44.16.2", {"start": v(73.66, 11.9) * mm, "end": v(73.27, 11.64) * mm});
            skLineSegment(sketch, "E44.17.0", {"start": v(73.3, 12.2) * mm, "end": v(73.66, 11.88) * mm});
            skLineSegment(sketch, "E44.17.1", {"start": v(73.66, 11.88) * mm, "end": v(73.6, 12.57) * mm});
            skLineSegment(sketch, "E44.17.2", {"start": v(73.6, 12.57) * mm, "end": v(73.3, 12.2) * mm});
            skLineSegment(sketch, "E44.18.0", {"start": v(73.17, 12.75) * mm, "end": v(73.6, 12.55) * mm});
            skLineSegment(sketch, "E44.18.1", {"start": v(73.6, 12.55) * mm, "end": v(73.34, 13.2) * mm});
            skLineSegment(sketch, "E44.18.2", {"start": v(73.34, 13.2) * mm, "end": v(73.17, 12.75) * mm});
            skLineSegment(sketch, "E44.19.0", {"start": v(72.88, 13.23) * mm, "end": v(73.35, 13.17) * mm});
            skLineSegment(sketch, "E44.19.1", {"start": v(73.35, 13.17) * mm, "end": v(72.9, 13.7) * mm});
            skLineSegment(sketch, "E44.19.2", {"start": v(72.9, 13.7) * mm, "end": v(72.88, 13.23) * mm});
            skSolve(sketch);
        }
        {
            var Q0;
            {var subQ0=sQuery(id+"F7.wireOp",EDGE,"E37.11.2");var subQ1=sQuery(id+"F7.wireOp",EDGE,"E30.0");var subQ2=makeQuery(id+"F7.imprint","INTERSECT",VERTEX,{"derivedFrom":[subQ1,subQ0]});Q0=makeQuery(id+"F7.imprint","IMPRINT",FACE,{"disambiguationData":[TD([[makeQuery(id+"F7.imprint","IMPRINT",EDGE,{"disambiguationData":[TD([[subQ2,-1.0]])],"derivedFrom":subQ1}),-1.0]])]});}
            var Q1;
            {var subQ0=sQuery(id+"F7.wireOp",EDGE,"E37.9.2");var subQ1=sQuery(id+"F7.wireOp",EDGE,"E30.0");var subQ2=makeQuery(id+"F7.imprint","INTERSECT",VERTEX,{"derivedFrom":[subQ1,subQ0]});Q1=makeQuery(id+"F7.imprint","IMPRINT",FACE,{"disambiguationData":[TD([[makeQuery(id+"F7.imprint","IMPRINT",EDGE,{"disambiguationData":[TD([[subQ2,-1.0]])],"derivedFrom":subQ1}),-1.0]])]});}
            var Q2;
            {var subQ0=sQuery(id+"F7.wireOp",EDGE,"E37.3.2");var subQ1=sQuery(id+"F7.wireOp",EDGE,"E30.0");var subQ2=makeQuery(id+"F7.imprint","INTERSECT",VERTEX,{"derivedFrom":[subQ1,subQ0]});Q2=makeQuery(id+"F7.imprint","IMPRINT",FACE,{"disambiguationData":[TD([[makeQuery(id+"F7.imprint","IMPRINT",EDGE,{"disambiguationData":[TD([[subQ2,-1.0]])],"derivedFrom":subQ1}),-1.0]])]});}
            var Q3;
            {var subQ0=sQuery(id+"F7.wireOp",EDGE,"E37.10.2");var subQ1=sQuery(id+"F7.wireOp",EDGE,"E30.0");var subQ2=makeQuery(id+"F7.imprint","INTERSECT",VERTEX,{"derivedFrom":[subQ1,subQ0]});Q3=makeQuery(id+"F7.imprint","IMPRINT",FACE,{"disambiguationData":[TD([[makeQuery(id+"F7.imprint","IMPRINT",EDGE,{"disambiguationData":[TD([[subQ2,-1.0]])],"derivedFrom":subQ1}),-1.0]])]});}
            var Q4;
            {var subQ0=sQuery(id+"F7.wireOp",EDGE,"E37.17.2");var subQ1=sQuery(id+"F7.wireOp",EDGE,"E30.0");var subQ2=makeQuery(id+"F7.imprint","INTERSECT",VERTEX,{"derivedFrom":[subQ1,subQ0]});Q4=makeQuery(id+"F7.imprint","IMPRINT",FACE,{"disambiguationData":[TD([[makeQuery(id+"F7.imprint","IMPRINT",EDGE,{"disambiguationData":[TD([[subQ2,-1.0]])],"derivedFrom":subQ1}),-1.0]])]});}
            var Q5;
            {var subQ0=sQuery(id+"F7.wireOp",EDGE,"E37.13.2");var subQ1=sQuery(id+"F7.wireOp",EDGE,"E30.0");var subQ2=makeQuery(id+"F7.imprint","INTERSECT",VERTEX,{"derivedFrom":[subQ1,subQ0]});Q5=makeQuery(id+"F7.imprint","IMPRINT",FACE,{"disambiguationData":[TD([[makeQuery(id+"F7.imprint","IMPRINT",EDGE,{"disambiguationData":[TD([[subQ2,-1.0]])],"derivedFrom":subQ1}),-1.0]])]});}
            var Q6;
            {var subQ0=sQuery(id+"F7.wireOp",EDGE,"E37.4.2");var subQ1=sQuery(id+"F7.wireOp",EDGE,"E30.0");var subQ2=makeQuery(id+"F7.imprint","INTERSECT",VERTEX,{"derivedFrom":[subQ1,subQ0]});Q6=makeQuery(id+"F7.imprint","IMPRINT",FACE,{"disambiguationData":[TD([[makeQuery(id+"F7.imprint","IMPRINT",EDGE,{"disambiguationData":[TD([[subQ2,-1.0]])],"derivedFrom":subQ1}),-1.0]])]});}
            var Q7;
            {var subQ0=sQuery(id+"F7.wireOp",EDGE,"E37.6.2");var subQ1=sQuery(id+"F7.wireOp",EDGE,"E30.0");var subQ2=makeQuery(id+"F7.imprint","INTERSECT",VERTEX,{"derivedFrom":[subQ1,subQ0]});Q7=makeQuery(id+"F7.imprint","IMPRINT",FACE,{"disambiguationData":[TD([[makeQuery(id+"F7.imprint","IMPRINT",EDGE,{"disambiguationData":[TD([[subQ2,-1.0]])],"derivedFrom":subQ1}),-1.0]])]});}
            var Q8;
            {var subQ0=sQuery(id+"F7.wireOp",EDGE,"E37.14.2");var subQ1=sQuery(id+"F7.wireOp",EDGE,"E30.0");var subQ2=makeQuery(id+"F7.imprint","INTERSECT",VERTEX,{"derivedFrom":[subQ1,subQ0]});Q8=makeQuery(id+"F7.imprint","IMPRINT",FACE,{"disambiguationData":[TD([[makeQuery(id+"F7.imprint","IMPRINT",EDGE,{"disambiguationData":[TD([[subQ2,-1.0]])],"derivedFrom":subQ1}),-1.0]])]});}
            var Q9;
            {var subQ0=sQuery(id+"F7.wireOp",EDGE,"E37.8.2");var subQ1=sQuery(id+"F7.wireOp",EDGE,"E30.0");var subQ2=makeQuery(id+"F7.imprint","INTERSECT",VERTEX,{"derivedFrom":[subQ1,subQ0]});Q9=makeQuery(id+"F7.imprint","IMPRINT",FACE,{"disambiguationData":[TD([[makeQuery(id+"F7.imprint","IMPRINT",EDGE,{"disambiguationData":[TD([[subQ2,-1.0]])],"derivedFrom":subQ1}),-1.0]])]});}
            var Q10;
            {var subQ0=sQuery(id+"F7.wireOp",EDGE,"E37.16.2");var subQ1=sQuery(id+"F7.wireOp",EDGE,"E30.0");var subQ2=makeQuery(id+"F7.imprint","INTERSECT",VERTEX,{"derivedFrom":[subQ1,subQ0]});Q10=makeQuery(id+"F7.imprint","IMPRINT",FACE,{"disambiguationData":[TD([[makeQuery(id+"F7.imprint","IMPRINT",EDGE,{"disambiguationData":[TD([[subQ2,-1.0]])],"derivedFrom":subQ1}),-1.0]])]});}
            var Q11;
            {var subQ0=sQuery(id+"F7.wireOp",EDGE,"E37.19.2");var subQ1=sQuery(id+"F7.wireOp",EDGE,"E30.0");var subQ2=makeQuery(id+"F7.imprint","INTERSECT",VERTEX,{"derivedFrom":[subQ1,subQ0]});Q11=makeQuery(id+"F7.imprint","IMPRINT",FACE,{"disambiguationData":[TD([[makeQuery(id+"F7.imprint","IMPRINT",EDGE,{"disambiguationData":[TD([[subQ2,-1.0]])],"derivedFrom":subQ1}),-1.0]])]});}
            var Q12;
            {var subQ0=sQuery(id+"F7.wireOp",EDGE,"E32");var subQ1=sQuery(id+"F7.wireOp",EDGE,"E30.0");var subQ2=makeQuery(id+"F7.imprint","INTERSECT",VERTEX,{"derivedFrom":[subQ1,subQ0]});Q12=makeQuery(id+"F7.imprint","IMPRINT",FACE,{"disambiguationData":[TD([[makeQuery(id+"F7.imprint","IMPRINT",EDGE,{"disambiguationData":[TD([[subQ2,-1.0]])],"derivedFrom":subQ1}),-1.0]])]});}
            var Q13;
            {var subQ0=sQuery(id+"F7.wireOp",EDGE,"E37.12.2");var subQ1=sQuery(id+"F7.wireOp",EDGE,"E30.0");var subQ2=makeQuery(id+"F7.imprint","INTERSECT",VERTEX,{"derivedFrom":[subQ1,subQ0]});Q13=makeQuery(id+"F7.imprint","IMPRINT",FACE,{"disambiguationData":[TD([[makeQuery(id+"F7.imprint","IMPRINT",EDGE,{"disambiguationData":[TD([[subQ2,-1.0]])],"derivedFrom":subQ1}),-1.0]])]});}
            var Q14;
            {var subQ0=sQuery(id+"F7.wireOp",EDGE,"E37.18.2");var subQ1=sQuery(id+"F7.wireOp",EDGE,"E30.0");var subQ2=makeQuery(id+"F7.imprint","INTERSECT",VERTEX,{"derivedFrom":[subQ1,subQ0]});Q14=makeQuery(id+"F7.imprint","IMPRINT",FACE,{"disambiguationData":[TD([[makeQuery(id+"F7.imprint","IMPRINT",EDGE,{"disambiguationData":[TD([[subQ2,-1.0]])],"derivedFrom":subQ1}),-1.0]])]});}
            var Q15;
            {var subQ0=sQuery(id+"F7.wireOp",EDGE,"E37.7.2");var subQ1=sQuery(id+"F7.wireOp",EDGE,"E30.0");var subQ2=makeQuery(id+"F7.imprint","INTERSECT",VERTEX,{"derivedFrom":[subQ1,subQ0]});Q15=makeQuery(id+"F7.imprint","IMPRINT",FACE,{"disambiguationData":[TD([[makeQuery(id+"F7.imprint","IMPRINT",EDGE,{"disambiguationData":[TD([[subQ2,-1.0]])],"derivedFrom":subQ1}),-1.0]])]});}
            var Q16;
            {var subQ0=sQuery(id+"F7.wireOp",EDGE,"E37.5.2");var subQ1=sQuery(id+"F7.wireOp",EDGE,"E30.0");var subQ2=makeQuery(id+"F7.imprint","INTERSECT",VERTEX,{"derivedFrom":[subQ1,subQ0]});Q16=makeQuery(id+"F7.imprint","IMPRINT",FACE,{"disambiguationData":[TD([[makeQuery(id+"F7.imprint","IMPRINT",EDGE,{"disambiguationData":[TD([[subQ2,-1.0]])],"derivedFrom":subQ1}),-1.0]])]});}
            var Q17;
            {var subQ0=sQuery(id+"F7.wireOp",EDGE,"E37.2.2");var subQ1=sQuery(id+"F7.wireOp",EDGE,"E30.0");var subQ2=makeQuery(id+"F7.imprint","INTERSECT",VERTEX,{"derivedFrom":[subQ1,subQ0]});Q17=makeQuery(id+"F7.imprint","IMPRINT",FACE,{"disambiguationData":[TD([[makeQuery(id+"F7.imprint","IMPRINT",EDGE,{"disambiguationData":[TD([[subQ2,-1.0]])],"derivedFrom":subQ1}),-1.0]])]});}
            var Q18;
            {var subQ0=sQuery(id+"F7.wireOp",EDGE,"E37.1.2");var subQ1=sQuery(id+"F7.wireOp",EDGE,"E30.0");var subQ2=makeQuery(id+"F7.imprint","INTERSECT",VERTEX,{"derivedFrom":[subQ1,subQ0]});Q18=makeQuery(id+"F7.imprint","IMPRINT",FACE,{"disambiguationData":[TD([[makeQuery(id+"F7.imprint","IMPRINT",EDGE,{"disambiguationData":[TD([[subQ2,-1.0]])],"derivedFrom":subQ1}),-1.0]])]});}
            var Q19;
            Q19=makeQuery(id+"F7.imprint","IMPRINT",FACE,{"disambiguationData":[TD([[makeQuery(id+"F7.imprint","IMPRINT",EDGE,{"derivedFrom":sQuery(id+"F7.wireOp",EDGE,"E27")}),-1.0]])]});
            var Q20;
            {var subQ0=sQuery(id+"F7.wireOp",EDGE,"E37.15.0");var subQ1=sQuery(id+"F7.wireOp",EDGE,"E30.0");var subQ2=makeQuery(id+"F7.imprint","INTERSECT",VERTEX,{"derivedFrom":[subQ1,subQ0]});Q20=makeQuery(id+"F7.imprint","IMPRINT",FACE,{"disambiguationData":[TD([[makeQuery(id+"F7.imprint","IMPRINT",EDGE,{"disambiguationData":[TD([[subQ2,1.0]])],"derivedFrom":subQ1}),-1.0]])]});}
            var Q21;
            {var subQ5=sQuery(id+"F7.wireOp",EDGE,"E37.3.1");Q21=makeQuery(id+"F7.imprint","IMPRINT",FACE,{"disambiguationData":[TD([[makeQuery(id+"F7.imprint","IMPRINT",EDGE,{"derivedFrom":subQ5}),-1.0]])]});}
            var Q22;
            {var subQ5=sQuery(id+"F7.wireOp",EDGE,"E37.17.1");Q22=makeQuery(id+"F7.imprint","IMPRINT",FACE,{"disambiguationData":[TD([[makeQuery(id+"F7.imprint","IMPRINT",EDGE,{"derivedFrom":subQ5}),-1.0]])]});}
            var Q23;
            {var subQ5=sQuery(id+"F7.wireOp",EDGE,"E37.1.1");Q23=makeQuery(id+"F7.imprint","IMPRINT",FACE,{"disambiguationData":[TD([[makeQuery(id+"F7.imprint","IMPRINT",EDGE,{"derivedFrom":subQ5}),-1.0]])]});}
            var Q24;
            {var subQ5=sQuery(id+"F7.wireOp",EDGE,"E37.4.1");Q24=makeQuery(id+"F7.imprint","IMPRINT",FACE,{"disambiguationData":[TD([[makeQuery(id+"F7.imprint","IMPRINT",EDGE,{"derivedFrom":subQ5}),-1.0]])]});}
            var Q25;
            {var subQ5=sQuery(id+"F7.wireOp",EDGE,"E37.5.1");Q25=makeQuery(id+"F7.imprint","IMPRINT",FACE,{"disambiguationData":[TD([[makeQuery(id+"F7.imprint","IMPRINT",EDGE,{"derivedFrom":subQ5}),-1.0]])]});}
            var Q26;
            {var subQ5=sQuery(id+"F7.wireOp",EDGE,"E37.12.1");Q26=makeQuery(id+"F7.imprint","IMPRINT",FACE,{"disambiguationData":[TD([[makeQuery(id+"F7.imprint","IMPRINT",EDGE,{"derivedFrom":subQ5}),-1.0]])]});}
            var Q27;
            {var subQ5=sQuery(id+"F7.wireOp",EDGE,"E37.16.1");Q27=makeQuery(id+"F7.imprint","IMPRINT",FACE,{"disambiguationData":[TD([[makeQuery(id+"F7.imprint","IMPRINT",EDGE,{"derivedFrom":subQ5}),-1.0]])]});}
            var Q28;
            {var subQ5=sQuery(id+"F7.wireOp",EDGE,"E37.9.1");Q28=makeQuery(id+"F7.imprint","IMPRINT",FACE,{"disambiguationData":[TD([[makeQuery(id+"F7.imprint","IMPRINT",EDGE,{"derivedFrom":subQ5}),-1.0]])]});}
            var Q29;
            {var subQ5=sQuery(id+"F7.wireOp",EDGE,"E37.6.1");Q29=makeQuery(id+"F7.imprint","IMPRINT",FACE,{"disambiguationData":[TD([[makeQuery(id+"F7.imprint","IMPRINT",EDGE,{"derivedFrom":subQ5}),-1.0]])]});}
            var Q30;
            {var subQ5=sQuery(id+"F7.wireOp",EDGE,"E37.18.1");Q30=makeQuery(id+"F7.imprint","IMPRINT",FACE,{"disambiguationData":[TD([[makeQuery(id+"F7.imprint","IMPRINT",EDGE,{"derivedFrom":subQ5}),-1.0]])]});}
            var Q31;
            {var subQ5=sQuery(id+"F7.wireOp",EDGE,"E37.7.1");Q31=makeQuery(id+"F7.imprint","IMPRINT",FACE,{"disambiguationData":[TD([[makeQuery(id+"F7.imprint","IMPRINT",EDGE,{"derivedFrom":subQ5}),-1.0]])]});}
            var Q32;
            {var subQ5=sQuery(id+"F7.wireOp",EDGE,"E37.14.1");Q32=makeQuery(id+"F7.imprint","IMPRINT",FACE,{"disambiguationData":[TD([[makeQuery(id+"F7.imprint","IMPRINT",EDGE,{"derivedFrom":subQ5}),-1.0]])]});}
            var Q33;
            {var subQ5=sQuery(id+"F7.wireOp",EDGE,"E37.11.1");Q33=makeQuery(id+"F7.imprint","IMPRINT",FACE,{"disambiguationData":[TD([[makeQuery(id+"F7.imprint","IMPRINT",EDGE,{"derivedFrom":subQ5}),-1.0]])]});}
            var Q34;
            {var subQ5=sQuery(id+"F7.wireOp",EDGE,"E37.19.1");Q34=makeQuery(id+"F7.imprint","IMPRINT",FACE,{"disambiguationData":[TD([[makeQuery(id+"F7.imprint","IMPRINT",EDGE,{"derivedFrom":subQ5}),-1.0]])]});}
            var Q35;
            {var subQ5=sQuery(id+"F7.wireOp",EDGE,"E37.2.1");Q35=makeQuery(id+"F7.imprint","IMPRINT",FACE,{"disambiguationData":[TD([[makeQuery(id+"F7.imprint","IMPRINT",EDGE,{"derivedFrom":subQ5}),-1.0]])]});}
            var Q36;
            {var subQ5=sQuery(id+"F7.wireOp",EDGE,"E37.8.1");Q36=makeQuery(id+"F7.imprint","IMPRINT",FACE,{"disambiguationData":[TD([[makeQuery(id+"F7.imprint","IMPRINT",EDGE,{"derivedFrom":subQ5}),-1.0]])]});}
            var Q37;
            {var subQ5=sQuery(id+"F7.wireOp",EDGE,"E37.13.1");Q37=makeQuery(id+"F7.imprint","IMPRINT",FACE,{"disambiguationData":[TD([[makeQuery(id+"F7.imprint","IMPRINT",EDGE,{"derivedFrom":subQ5}),-1.0]])]});}
            var Q38;
            {var subQ5=sQuery(id+"F7.wireOp",EDGE,"E33");Q38=makeQuery(id+"F7.imprint","IMPRINT",FACE,{"disambiguationData":[TD([[makeQuery(id+"F7.imprint","IMPRINT",EDGE,{"derivedFrom":subQ5}),-1.0]])]});}
            var Q39;
            {var subQ5=sQuery(id+"F7.wireOp",EDGE,"E37.15.1");Q39=makeQuery(id+"F7.imprint","IMPRINT",FACE,{"disambiguationData":[TD([[makeQuery(id+"F7.imprint","IMPRINT",EDGE,{"derivedFrom":subQ5}),-1.0]])]});}
            var Q40;
            {var subQ5=sQuery(id+"F7.wireOp",EDGE,"E37.10.1");Q40=makeQuery(id+"F7.imprint","IMPRINT",FACE,{"disambiguationData":[TD([[makeQuery(id+"F7.imprint","IMPRINT",EDGE,{"derivedFrom":subQ5}),-1.0]])]});}
            var Q41;
            Q41=makeQuery(id+"F7.imprint","IMPRINT",FACE,{"disambiguationData":[TD([[makeQuery(id+"F7.imprint","IMPRINT",EDGE,{"derivedFrom":sQuery(id+"F7.wireOp",EDGE,"E27")}),1.0]])]});
            extrude(context, id + "F8", {"entities" : qUnion([Q0, Q1, Q2, Q3, Q4, Q5, Q6, Q7, Q8, Q9, Q10, Q11, Q12, Q13, Q14, Q15, Q16, Q17, Q18, Q19, Q20, Q21, Q22, Q23, Q24, Q25, Q26, Q27, Q28, Q29, Q30, Q31, Q32, Q33, Q34, Q35, Q36, Q37, Q38, Q39, Q40, Q41]), "depth" : 40 * mm});
        }
    });
